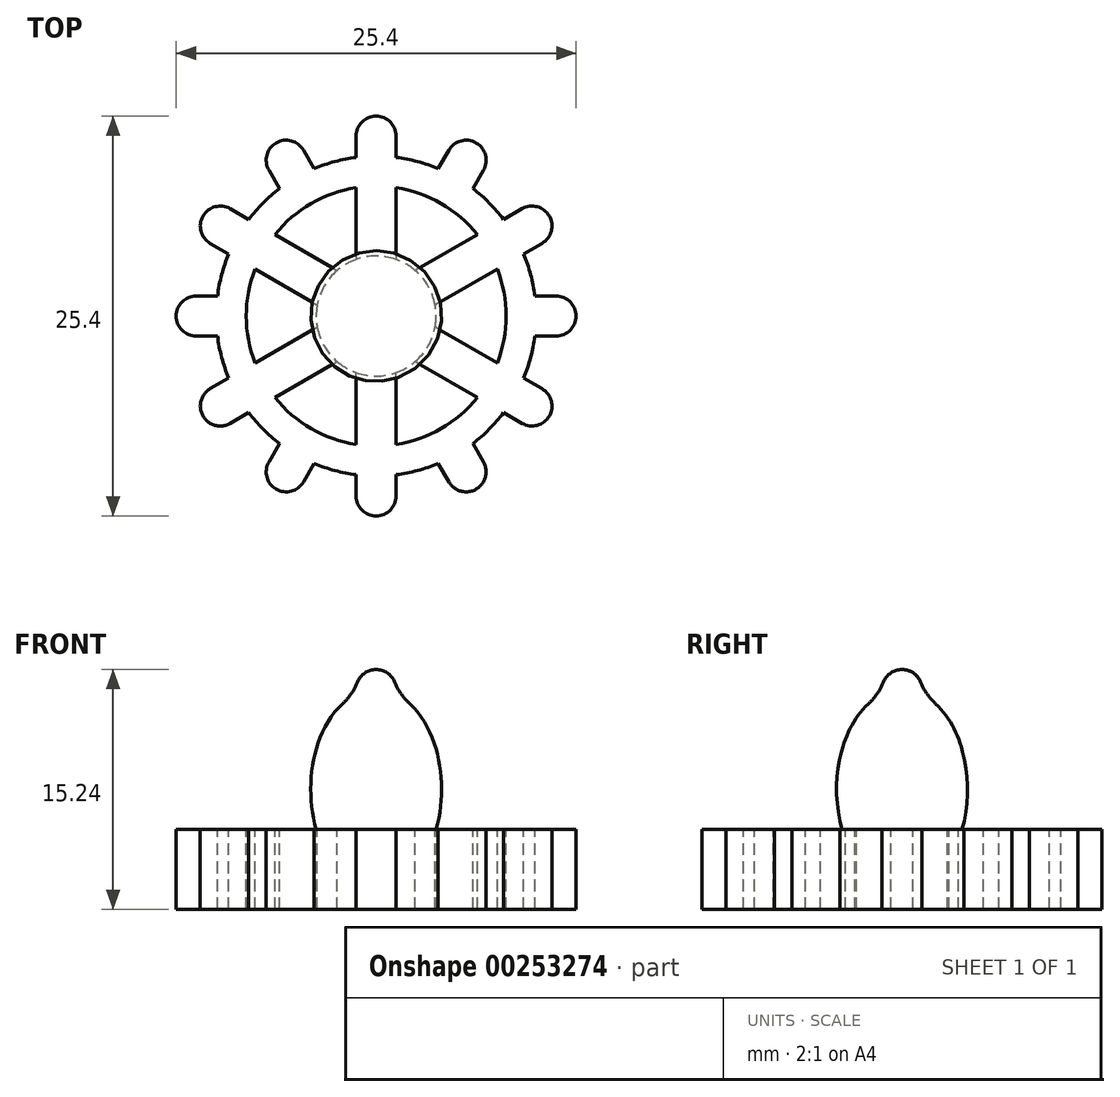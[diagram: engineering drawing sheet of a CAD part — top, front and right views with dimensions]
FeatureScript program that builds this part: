
annotation { "Feature Type Name" : "Feature", "Feature Type Description" : "" }
export const myFeature = defineFeature(function(context is Context, id is Id, definition is map)
    precondition{}
    {
        {
            var Q0;
            Q0=qCreatedBy(makeId("Top.planeOp"),FACE);
            var sketch = newSketch(context, id + "F0", { "sketchPlane" : qUnion([Q0])});
            skArc(sketch, "E0", {"start": v(-1.27, 10.08) * mm, "mid": v(-2.63, 9.81) * mm, "end": v(-3.94, 9.36) * mm});
            skLineSegment(sketch, "E1", {"start": v(0, 10.16) * mm, "end": v(0, 11.43) * mm, "construction": true});
            skArc(sketch, "E2", {"start": v(1.27, 11.43) * mm, "mid": v(0, 12.7) * mm, "end": v(-1.27, 11.43) * mm});
            skLineSegment(sketch, "E3", {"start": v(-1.27, 11.43) * mm, "end": v(-1.27, 10.08) * mm});
            skLineSegment(sketch, "E4", {"start": v(1.27, 11.43) * mm, "end": v(1.27, 10.08) * mm});
            skLineSegment(sketch, "E5.1.0", {"start": v(-6.81, 9.26) * mm, "end": v(-6.14, 8.1) * mm});
            skArc(sketch, "E5.1.1", {"start": v(-4.62, 10.53) * mm, "mid": v(-6.35, 11) * mm, "end": v(-6.81, 9.26) * mm});
            skLineSegment(sketch, "E5.1.2", {"start": v(-4.62, 10.53) * mm, "end": v(-3.94, 9.36) * mm});
            skLineSegment(sketch, "E5.2.0", {"start": v(-10.53, 4.62) * mm, "end": v(-9.36, 3.94) * mm});
            skArc(sketch, "E5.2.1", {"start": v(-9.26, 6.81) * mm, "mid": v(-11, 6.35) * mm, "end": v(-10.53, 4.62) * mm});
            skLineSegment(sketch, "E5.2.2", {"start": v(-9.26, 6.81) * mm, "end": v(-8.1, 6.14) * mm});
            skLineSegment(sketch, "E5.3.0", {"start": v(-11.43, -1.27) * mm, "end": v(-10.08, -1.27) * mm});
            skArc(sketch, "E5.3.1", {"start": v(-11.43, 1.27) * mm, "mid": v(-12.7, 0) * mm, "end": v(-11.43, -1.27) * mm});
            skLineSegment(sketch, "E5.3.2", {"start": v(-11.43, 1.27) * mm, "end": v(-10.08, 1.27) * mm});
            skLineSegment(sketch, "E5.4.0", {"start": v(-9.26, -6.81) * mm, "end": v(-8.1, -6.14) * mm});
            skArc(sketch, "E5.4.1", {"start": v(-10.53, -4.62) * mm, "mid": v(-11, -6.35) * mm, "end": v(-9.26, -6.81) * mm});
            skLineSegment(sketch, "E5.4.2", {"start": v(-10.53, -4.62) * mm, "end": v(-9.36, -3.94) * mm});
            skLineSegment(sketch, "E5.5.0", {"start": v(-4.62, -10.53) * mm, "end": v(-3.94, -9.36) * mm});
            skArc(sketch, "E5.5.1", {"start": v(-6.81, -9.26) * mm, "mid": v(-6.35, -11) * mm, "end": v(-4.62, -10.53) * mm});
            skLineSegment(sketch, "E5.5.2", {"start": v(-6.81, -9.26) * mm, "end": v(-6.14, -8.1) * mm});
            skLineSegment(sketch, "E5.6.0", {"start": v(1.27, -11.43) * mm, "end": v(1.27, -10.08) * mm});
            skArc(sketch, "E5.6.1", {"start": v(-1.27, -11.43) * mm, "mid": v(0, -12.7) * mm, "end": v(1.27, -11.43) * mm});
            skLineSegment(sketch, "E5.6.2", {"start": v(-1.27, -11.43) * mm, "end": v(-1.27, -10.08) * mm});
            skLineSegment(sketch, "E5.7.0", {"start": v(6.81, -9.26) * mm, "end": v(6.14, -8.1) * mm});
            skArc(sketch, "E5.7.1", {"start": v(4.62, -10.53) * mm, "mid": v(6.35, -11) * mm, "end": v(6.81, -9.26) * mm});
            skLineSegment(sketch, "E5.7.2", {"start": v(4.62, -10.53) * mm, "end": v(3.94, -9.36) * mm});
            skLineSegment(sketch, "E5.8.0", {"start": v(10.53, -4.62) * mm, "end": v(9.36, -3.94) * mm});
            skArc(sketch, "E5.8.1", {"start": v(9.26, -6.81) * mm, "mid": v(11, -6.35) * mm, "end": v(10.53, -4.62) * mm});
            skLineSegment(sketch, "E5.8.2", {"start": v(9.26, -6.81) * mm, "end": v(8.1, -6.14) * mm});
            skLineSegment(sketch, "E5.9.0", {"start": v(11.43, 1.27) * mm, "end": v(10.08, 1.27) * mm});
            skArc(sketch, "E5.9.1", {"start": v(11.43, -1.27) * mm, "mid": v(12.7, 0) * mm, "end": v(11.43, 1.27) * mm});
            skLineSegment(sketch, "E5.9.2", {"start": v(11.43, -1.27) * mm, "end": v(10.08, -1.27) * mm});
            skLineSegment(sketch, "E5.10.0", {"start": v(9.26, 6.81) * mm, "end": v(8.1, 6.14) * mm});
            skArc(sketch, "E5.10.1", {"start": v(10.53, 4.62) * mm, "mid": v(11, 6.35) * mm, "end": v(9.26, 6.81) * mm});
            skLineSegment(sketch, "E5.10.2", {"start": v(10.53, 4.62) * mm, "end": v(9.36, 3.94) * mm});
            skLineSegment(sketch, "E5.11.0", {"start": v(4.62, 10.53) * mm, "end": v(3.94, 9.36) * mm});
            skArc(sketch, "E5.11.1", {"start": v(6.81, 9.26) * mm, "mid": v(6.35, 11) * mm, "end": v(4.62, 10.53) * mm});
            skLineSegment(sketch, "E5.11.2", {"start": v(6.81, 9.26) * mm, "end": v(6.14, 8.1) * mm});
            skArc(sketch, "E6.trimOffspring", {"start": v(-6.14, 8.1) * mm, "mid": v(-7.18, 7.18) * mm, "end": v(-8.1, 6.14) * mm});
            skArc(sketch, "E7.trimOffspring", {"start": v(-9.36, 3.94) * mm, "mid": v(-9.81, 2.63) * mm, "end": v(-10.08, 1.27) * mm});
            skArc(sketch, "E8.trimOffspring", {"start": v(-10.08, -1.27) * mm, "mid": v(-9.81, -2.63) * mm, "end": v(-9.36, -3.94) * mm});
            skArc(sketch, "E9.trimOffspring", {"start": v(-8.1, -6.14) * mm, "mid": v(-7.18, -7.18) * mm, "end": v(-6.14, -8.1) * mm});
            skArc(sketch, "E10.trimOffspring", {"start": v(-3.94, -9.36) * mm, "mid": v(-2.63, -9.81) * mm, "end": v(-1.27, -10.08) * mm});
            skArc(sketch, "E11.trimOffspring", {"start": v(1.27, -10.08) * mm, "mid": v(2.63, -9.81) * mm, "end": v(3.94, -9.36) * mm});
            skArc(sketch, "E12.trimOffspring", {"start": v(6.14, -8.1) * mm, "mid": v(7.18, -7.18) * mm, "end": v(8.1, -6.14) * mm});
            skArc(sketch, "E13.trimOffspring", {"start": v(9.36, -3.94) * mm, "mid": v(9.81, -2.63) * mm, "end": v(10.08, -1.27) * mm});
            skArc(sketch, "E14.trimOffspring", {"start": v(10.08, 1.27) * mm, "mid": v(9.81, 2.63) * mm, "end": v(9.36, 3.94) * mm});
            skArc(sketch, "E15.trimOffspring", {"start": v(8.1, 6.14) * mm, "mid": v(7.18, 7.18) * mm, "end": v(6.14, 8.1) * mm});
            skArc(sketch, "E16.trimOffspring", {"start": v(3.94, 9.36) * mm, "mid": v(2.63, 9.81) * mm, "end": v(1.27, 10.08) * mm});
            skArc(sketch, "E17", {"start": v(-1.27, 8.16) * mm, "mid": v(-4.13, 7.15) * mm, "end": v(-6.43, 5.18) * mm});
            skLineSegment(sketch, "E18", {"start": v(-1.27, 8.16) * mm, "end": v(-1.27, 3.6) * mm});
            skArc(sketch, "E19", {"start": v(-3.75, 0.7) * mm, "mid": v(-3.81, 0) * mm, "end": v(-3.75, -0.7) * mm});
            skLineSegment(sketch, "E20.MirrorCS", {"start": v(1.27, 8.16) * mm, "end": v(1.27, 3.6) * mm});
            skLineSegment(sketch, "E21.1.0", {"start": v(-6.43, 5.18) * mm, "end": v(-2.48, 2.9) * mm});
            skLineSegment(sketch, "E21.1.1", {"start": v(-7.7, 2.98) * mm, "end": v(-3.75, 0.7) * mm});
            skLineSegment(sketch, "E21.2.0", {"start": v(-7.7, -2.98) * mm, "end": v(-3.75, -0.7) * mm});
            skLineSegment(sketch, "E21.2.1", {"start": v(-6.43, -5.18) * mm, "end": v(-2.48, -2.9) * mm});
            skLineSegment(sketch, "E21.3.0", {"start": v(-1.27, -8.16) * mm, "end": v(-1.27, -3.6) * mm});
            skLineSegment(sketch, "E21.3.1", {"start": v(1.27, -8.16) * mm, "end": v(1.27, -3.6) * mm});
            skLineSegment(sketch, "E21.4.0", {"start": v(6.43, -5.18) * mm, "end": v(2.48, -2.9) * mm});
            skLineSegment(sketch, "E21.4.1", {"start": v(7.7, -2.98) * mm, "end": v(3.75, -0.7) * mm});
            skLineSegment(sketch, "E21.5.0", {"start": v(7.7, 2.98) * mm, "end": v(3.75, 0.7) * mm});
            skLineSegment(sketch, "E21.5.1", {"start": v(6.43, 5.18) * mm, "end": v(2.48, 2.9) * mm});
            skArc(sketch, "E22.trimOffspring", {"start": v(-7.7, 2.98) * mm, "mid": v(-8.26, 0) * mm, "end": v(-7.7, -2.98) * mm});
            skArc(sketch, "E23.trimOffspring", {"start": v(2.48, 2.9) * mm, "mid": v(1.9, 3.3) * mm, "end": v(1.27, 3.6) * mm});
            skArc(sketch, "E24.trimOffspring", {"start": v(-1.27, 3.6) * mm, "mid": v(-1.9, 3.3) * mm, "end": v(-2.48, 2.9) * mm});
            skArc(sketch, "E25.trimOffspring", {"start": v(6.43, 5.18) * mm, "mid": v(4.13, 7.15) * mm, "end": v(1.27, 8.16) * mm});
            skArc(sketch, "E26.trimOffspring", {"start": v(3.75, -0.7) * mm, "mid": v(3.8, 0) * mm, "end": v(3.75, 0.7) * mm});
            skArc(sketch, "E27.trimOffspring", {"start": v(7.7, -2.98) * mm, "mid": v(8.26, 0) * mm, "end": v(7.7, 2.98) * mm});
            skArc(sketch, "E28.trimOffspring", {"start": v(1.27, -3.6) * mm, "mid": v(1.9, -3.3) * mm, "end": v(2.48, -2.9) * mm});
            skArc(sketch, "E29.trimOffspring", {"start": v(1.27, -8.16) * mm, "mid": v(4.13, -7.15) * mm, "end": v(6.43, -5.18) * mm});
            skArc(sketch, "E30.trimOffspring", {"start": v(-6.43, -5.18) * mm, "mid": v(-4.13, -7.15) * mm, "end": v(-1.27, -8.16) * mm});
            skArc(sketch, "E31.trimOffspring", {"start": v(-2.48, -2.9) * mm, "mid": v(-1.9, -3.3) * mm, "end": v(-1.27, -3.6) * mm});
            skSolve(sketch);
        }
        {
            var Q0;
            Q0 = qSketchRegion(id + "F0", true);
            extrude(context, id + "F1", {"entities" : qUnion([Q0]), "oppositeDirection" : true, "depth" : 1.27 * mm});
        }
        {
            var Q0;
            Q0 = qSketchRegion(id + "F0", true);
            extrude(context, id + "F2", {"entities" : qUnion([Q0]), "operationType" : NewBodyOperationType.ADD, "depth" : 3.8 * mm});
        }
        {
            var Q0;
            Q0=qCreatedBy(makeId("Right.planeOp"),FACE);
            var sketch = newSketch(context, id + "F3", { "sketchPlane" : qUnion([Q0])});
            skLineSegment(sketch, "E32", {"start": v(0, 3.8) * mm, "end": v(0, 6.35) * mm, "construction": true});
            skEllipticalArc(sketch, "E33", {});
            skLineSegment(sketch, "E34", {"start": v(0, 3.8) * mm, "end": v(3.81, 3.8) * mm, "construction": true});
            skPoint(sketch, "E35.centerSnap0", {"position": v(0, 12.7) * mm});
            skLineSegment(sketch, "E36", {"start": v(0, 12.7) * mm, "end": v(0, 3.8) * mm});
            skPoint(sketch, "E37.orphan", {"position": v(0, 14.65) * mm});
            skArc(sketch, "E38.trimOffspring", {"start": v(-0.64, 13.8) * mm, "mid": v(-0.96, 13.53) * mm, "end": v(-1.18, 13.18) * mm});
            skPoint(sketch, "E35.center.orphan", {"position": v(0, 12.7) * mm});
            skPoint(sketch, "E39.visualSharp", {"position": v(-1.24, 12.41) * mm});
            skArc(sketch, "E39.filletArc", {"start": v(-2.14, 11.8) * mm, "mid": v(-1.58, 12.43) * mm, "end": v(-1.18, 13.18) * mm});
            skPoint(sketch, "E40.visualSharp", {"position": v(0, 13.97) * mm});
            skArc(sketch, "E41.trimOffspring", {"start": v(0, 13.97) * mm, "mid": v(-0.33, 13.93) * mm, "end": v(-0.63, 13.8) * mm});
            skLineSegment(sketch, "E42", {"start": v(0, 12.7) * mm, "end": v(0, 13.97) * mm});
            skLineSegment(sketch, "E43", {"start": v(0, 3.8) * mm, "end": v(-3.81, 3.8) * mm});
            skPoint(sketch, "E44.orphan", {"position": v(0, 0) * mm});
            const initialGuessF3  = {"E33": [0, 0.00635, 0, -1, 0.00635, 0.004157050808995655, 3.6812308924390895, 5.1239058264521775]};
            skSetInitialGuess(sketch, initialGuessF3);
            skSolve(sketch);
        }
        {
            var Q0;
            Q0=makeQuery(id+"F3.imprint","IMPRINT",FACE,{"disambiguationData":[TD([[makeQuery(id+"F3.imprint","IMPRINT",EDGE,{"derivedFrom":sQuery(id+"F3.wireOp",EDGE,"E33")}),1.0]])]});
            var Q1;
            Q1=sQuery(id+"F3.wireOp",EDGE,"E36");
            revolve(context, id + "F4", {"operationType" : NewBodyOperationType.ADD, "entities" : qUnion([Q0]), "axis" : qUnion([Q1]), "revolveType" : RevolveType.FULL});
        }
    });
